# Revit family: acdc BLADE
name_source: partatom
category: Lighting Fixtures
revit_build: Autodesk Revit 2018 (Build: 20170223_1515(x64)
units: mm (PartAtom-declared; Revit-internal decimal feet)

## family parameters
Always vertical = No
Cut with Voids When Loaded = Yes
Light Source = Yes
Part Type = Normal
Room Calculation Point = No
Round Connector Dimension = Use Diameter
Shared = No
Work Plane-Based = Yes

## types (1)
- BL LRI L03 1200-830 M ABK LF 0 67 HFX
    Apparent Load = 18 VA
    Body = acdc_Metal_Black
    Color Filter = 16777215
    Cover = acdc_Cover_Self_llumination
    Default Elevation = 0 mm  [stored 0 ft]
    Dimming Lamp Color Temperature Shift = <None>
    Emit Shape Visible in Rendering = No
    Emit from Rectangle Length = 1219 mm
    Emit from Rectangle Width = 610 mm
    Frame = acdc_Metal_Aluminium
    Height = 124 mm  [stored 0.406824 ft]
    Length = 336 mm  [stored 1.10236 ft]
    Manufacturer = acdc Lighting
    Photometric Web File = acdc_BL_LRI_L03_1200-830_M_LF_0.ies
    Tilt Angle = -90.00°
    URL = https://www.acdclighting.com
    Voltage = 230 V
    Width = 80 mm  [stored 0.262467 ft]

note: [stored X ft] marks values corroborated as IEEE doubles in the binary element streams (Revit-internal decimal feet)

## geometry (parser evidence)
native form markers: Sweep x3
no freeform markers — native parametric forms only
